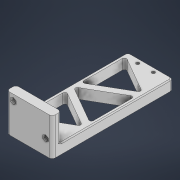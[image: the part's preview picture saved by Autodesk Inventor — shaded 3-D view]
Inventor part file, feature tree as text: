
AUTODESK INVENTOR PART (.ipt)
format: ipt  version: 2022 (Build 260153000, 153)  size: 246,784 bytes
history: native  units: mm
features: extrude x7, sketch x7, fillet x3, chamfer x2
ambient origin geometry x8: Origin, YZ Plane, XZ Plane, XY Plane, X Axis, Y Axis, Z Axis, Center Point
bodies: Solid1 (feature_tree)
feature tree (19):
  extrude  "Extrusion1"  Depth=10.0mm
  extrude  "Extrusion2"  Depth=9.0mm
  extrude  "Extrusion3"  Depth=6.5mm
  extrude  "Extrusion4"  Depth=3.2mm
  extrude  "Extrusion5"  Depth=32.0mm
  extrude  "Extrusion7"  Depth=27.0mm TaperAngle=0.0deg
  fillet  "Fillet1"  Radius=2.75mm
  fillet  "Fillet2"  Radius=2.75mm
  chamfer  "Chamfer1"  Distance=2.7mm
  chamfer  "Chamfer2"  Distance=7.75mm
  extrude  "Extrusion8"  Depth=2.0mm
  fillet  "Fillet3"  Radius=3.2mm
  sketch  "Sketch1"  dims[d0=45.0mm d1=10.0mm]
  sketch  "Sketch2"  dims[d2=120.0mm d3=0.0mm d4=9.0mm]
  sketch  "Sketch3"  dims[d5=27.0mm d6=0.0mm d7=6.5mm]
  sketch  "Sketch4"  dims[d8=5.0mm d9=3.2mm]
  sketch  "Sketch5"  dims[d10=16.0mm d11=32.0mm]
  sketch  "Sketch7"  dims[d12=3.2mm d13=27.0mm d14=0.0mm d15=2.75mm d16=2.75mm d17=2.7mm d18=0.0mm]
  sketch  "Sketch8"  dims[d19=5.0mm d20=7.75mm d21=15.5mm d22=3.2mm d23=3.2mm d24=10.0mm d25=0.0mm d30=5.9mm d31=5.9mm d32=5.0mm d33=0.0mm d34=3.0mm d35=3.0mm d36=0.5mm d37=2.0mm d38=45.0deg d39=1.0mm d40=2.0mm d41=45.0deg d42=5.0mm d44=3.0mm d45=180.0deg d47=30.0deg d48=60.0deg d49=7.0mm d50=120.0deg d51=60.0deg d52=2.0mm d53=10.0mm d54=0.0mm d55=7.0mm d56=90.0deg d64=30.0deg d65=60.0deg d66=2.0mm]
